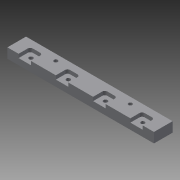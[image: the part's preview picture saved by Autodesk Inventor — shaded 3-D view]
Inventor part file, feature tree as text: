
AUTODESK INVENTOR PART (.ipt)
format: ipt  version: 2013 SP2 (Build 170200200, 200)  size: 141,312 bytes
history: native  units: mm
features: reference x4, extrude x3, sketch x3
ambient origin geometry x8: Origin, YZ Plane, XZ Plane, XY Plane, X Axis, Y Axis, Z Axis, Center Point
bodies: Solid1 (feature_tree)
feature tree (10):
  extrude  "Extrusion1"  Depth=15.0mm
  extrude  "Extrusion2"  Depth=3.2mm
  extrude  "Extrusion3"  Depth=3.2mm
  sketch  "Sketch1"  dims[d0=118.0mm d1=15.0mm]
  sketch  "Sketch2"  dims[d2=8.0mm d3=0.0mm d4=3.2mm]
  sketch  "Sketch3"  dims[d5=3.2mm d6=3.2mm d11=5.0mm d12=10.0mm d13=0.0mm d14=3.0mm d15=30.0mm d16=30.0mm d17=30.0mm d18=14.0mm d19=14.0mm d20=3.0mm d21=3.0mm d22=5.0mm d23=29.0mm d24=29.0mm d25=3.0mm d26=0.0mm]
  reference  "Reference1"
  reference  "Reference2"
  reference  "Reference3"
  reference  "Reference4"
